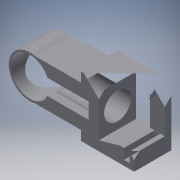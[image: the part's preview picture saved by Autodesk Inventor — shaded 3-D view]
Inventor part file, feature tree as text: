
AUTODESK INVENTOR PART (.ipt)
format: ipt  version: 2016 (Build 200138000, 138)  size: 249,856 bytes
history: native  units: mm
features: extrude x10, sketch x10, projected_geometry x2, reference x2
ambient origin geometry x8: Origin, YZ Plane, XZ Plane, XY Plane, X Axis, Y Axis, Z Axis, Center Point
bodies: Solid1 (feature_tree)
feature tree (24):
  extrude  "Extrusion1"  Depth=7.0mm
  extrude  "Extrusion2"  Depth=14.5mm TaperAngle=0.0deg
  extrude  "Extrusion3"  Depth=3.749999mm
  extrude  "Extrusion4"  Depth=20.0mm
  extrude  "Extrusion5"  Depth=15.0mm
  extrude  "Extrusion6"  Depth=14.0mm
  extrude  "Extrusion7"  Depth=10.5mm
  extrude  "Extrusion9"  Depth=1.0mm TaperAngle=0.0deg
  extrude  "Extrusion10"  Depth=3.0mm
  extrude  "Extrusion12"  Depth=3.0mm
  sketch  "Sketch1"  dims[d0=23.495mm d1=7.0mm]
  sketch  "Sketch2"  dims[d8=6.0mm d10=15.0mm d11=14.999996mm d16=14.5mm d17=0.0mm]
  sketch  "Sketch3"  dims[d18=3.749998mm d19=3.749999mm]
  sketch  "Sketch4"  dims[d20=20.0mm d21=0.0mm d22=16.5mm]
  sketch  "Sketch5"  dims[d23=14.5mm d24=0.0mm d25=15.0mm]
  sketch  "Sketch6"  dims[d26=10.5mm d27=0.0mm d28=14.0mm]
  sketch  "Sketch7"  dims[d29=10.5mm d30=0.0mm d31=10.5mm]
  sketch  "Sketch9"  dims[d32=30.0mm d33=0.0mm d34=1.0mm d35=0.0mm]
  sketch  "Sketch10"  dims[d39=3.0mm d40=3.0mm]
  projected_geometry  "Projected Loop1"
  projected_geometry  "Projected Loop2"
  reference  "Reference2"
  sketch  "Sketch12"  dims[d41=3.0mm d42=3.0mm d43=20.0mm d44=3.0mm d45=0.0mm d46=3.0mm d47=0.0mm d50=16.5mm d51=0.25mm d52=0.25mm d53=0.25mm d54=2.0mm d55=6.99mm d56=0.0mm]
  reference  "Reference3"
